# Revit family: Doors_Integrated_Double-Egress-Hold-Open-90_Total-Door
name_source: partatom
category: Doors
units: mm (PartAtom-declared; Revit-internal decimal feet)

## family parameters
Always vertical = Yes
Classification Number = 23.30.10.00
Cut with Voids When Loaded = No
Host = Wall
Room Calculation Point = No
Shared = No

## types (1)
- Doors_Integrated_Double-Egress-Hold-Open-90_Total-Door
    2D PLAN = 6' - 0"
    2D Panel Width = 2' - 11 23/32"
    Analytic Construction = <None>
    CAD Details = https://www.arcat.com
    Define Thermal Properties by = Schematic Type
    Frame Projection Ext. = 0' - 1"
    Frame Projection Int. = 0' - 1"
    Frame Width = 0' - 3"
    Function = Interior
    Height = 7' - 0"
    Keynote = 08 17 00
    Magnet Finish = Aluminium(1)
    Manufacturer = Total Door
    PANEL HEIGHT = 6' - 9 1/2"
    Panel Finish = Door Panel Finish
    Panel Width = 3' - 0"
    Product Page URL = https://www.arcat.com
    Push Panic Bar Finish = Aluminium
    Specification = https://www.arcat.com
    URL = https://totaldoor.com
    Wall Closure = By host
    Width = 6' - 2 1/4"

## geometry (parser evidence)
native form markers: Sweep x33
no freeform markers — native parametric forms only
